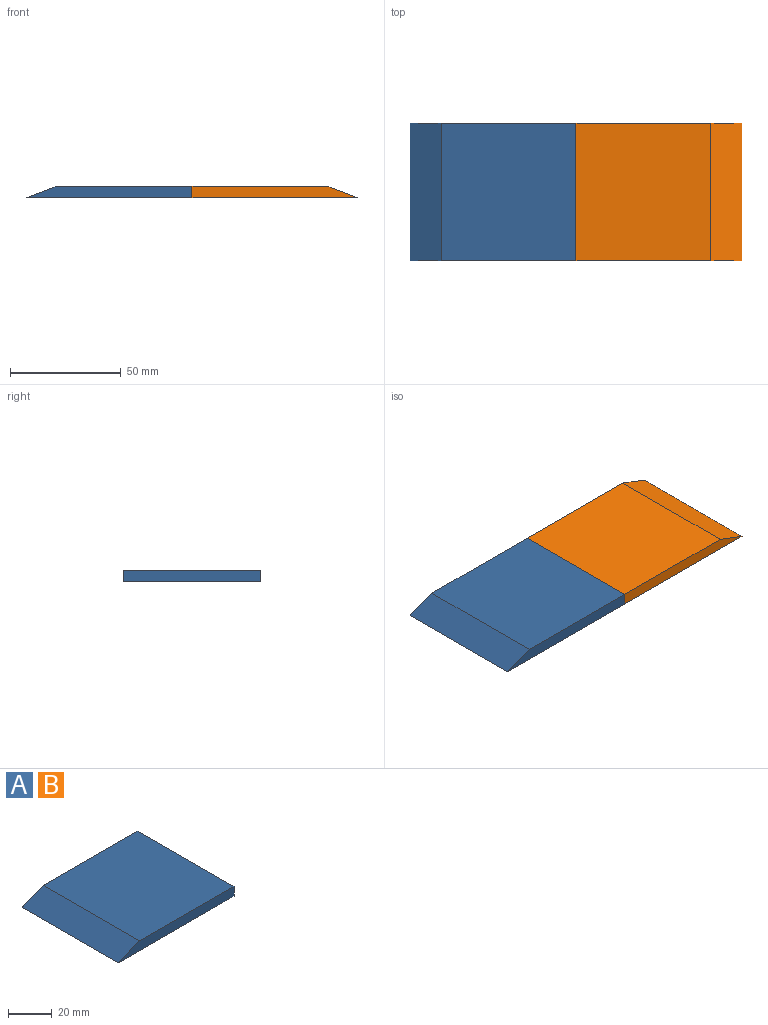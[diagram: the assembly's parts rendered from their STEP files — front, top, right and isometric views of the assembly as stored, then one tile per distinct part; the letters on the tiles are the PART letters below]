
ASSEMBLY  parts=2 mates=1
PART A: 6 faces, bbox 75x62.3x5.4 mm
  f0: plane 62.3x61mm, normal (0,0,1), area 3800.3mm2, adj f1,f3,f4,f5
  f1: plane 62.3x14mm, normal (-0.36,0,0.93), area 934.5mm2, adj f0,f2,f4,f5
  f2: plane 75x62.3mm, normal (0,0,-1), area 4672.5mm2, adj f1,f3,f4,f5
  f3: plane 62.3x5.39mm, normal (1,0,0), area 335.5mm2, adj f0,f2,f4,f5
  f4: plane 75x5.39mm, normal (0,-1,0), area 366.2mm2, adj f0,f1,f2,f3
  f5: plane 75x5.39mm, normal (0,1,0), area 366.2mm2, adj f0,f1,f2,f3
PART B: same geometry as A
PLACE A t=(7.46,22.37,-44.57)mm
PLACE B rot(axis=(0,0,1),180deg) t=(7.46,-39.93,-44.57)mm
MATE fastened B.f3 <-> A.f3  axis (-1,0,0) through (7.46,-8.78,-41.88)mm
